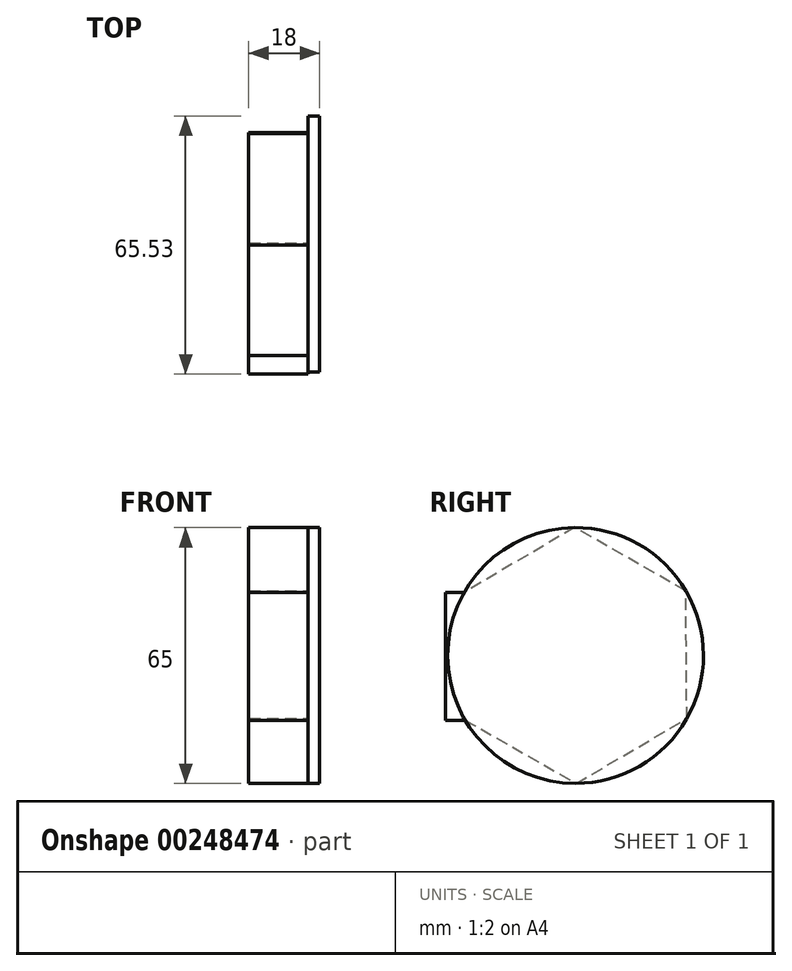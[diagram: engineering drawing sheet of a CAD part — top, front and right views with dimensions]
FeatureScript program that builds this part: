
annotation { "Feature Type Name" : "Feature", "Feature Type Description" : "" }
export const myFeature = defineFeature(function(context is Context, id is Id, definition is map)
    precondition{}
    {
        {
            var Q0;
            Q0=qCreatedBy(makeId("Right.planeOp"),FACE);
            var sketch = newSketch(context, id + "F0", { "sketchPlane" : qUnion([Q0])});
            skCircle(sketch, "E0", {"center": v(0, 0) * mm, "radius": 32.5 * mm});
            skSolve(sketch);
        }
        {
            var Q0;
            Q0 = qSketchRegion(id + "F0", true);
            extrude(context, id + "F1", {"entities" : qUnion([Q0]), "depth" : 3 * mm});
        }
        {
            var Q0;
            Q0=makeQuery(id+"F1.opExtrude","CAP_FACE",FACE,{"disambiguationData":[OSD([sQuery(id+"F0.wireOp",EDGE,"E0")])],"isStart":true});
            var sketch = newSketch(context, id + "F2", { "sketchPlane" : qUnion([Q0])});
            skLineSegment(sketch, "E1", {"start": v(28.26, 16.05) * mm, "end": v(33.03, 16.05) * mm});
            skLineSegment(sketch, "E2", {"start": v(33.03, 16.05) * mm, "end": v(33.03, -16.45) * mm});
            skLineSegment(sketch, "E3", {"start": v(33.03, -16.45) * mm, "end": v(28.03, -16.45) * mm});
            skLineSegment(sketch, "E4", {"start": v(28.03, -16.45) * mm, "end": v(-0.23, -32.5) * mm});
            skLineSegment(sketch, "E5", {"start": v(-0.23, -32.5) * mm, "end": v(-28.26, -16.05) * mm});
            skLineSegment(sketch, "E6", {"start": v(-28.26, -16.05) * mm, "end": v(-28.03, 16.45) * mm});
            skLineSegment(sketch, "E7", {"start": v(-28.03, 16.45) * mm, "end": v(0.23, 32.5) * mm});
            skLineSegment(sketch, "E8", {"start": v(0.23, 32.5) * mm, "end": v(28.26, 16.05) * mm});
            skSolve(sketch);
        }
        {
            var Q0;
            Q0 = qSketchRegion(id + "F2", true);
            extrude(context, id + "F3", {"entities" : qUnion([Q0]), "operationType" : NewBodyOperationType.ADD, "depth" : 15 * mm});
        }
    });
